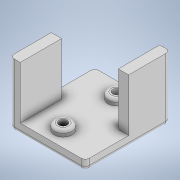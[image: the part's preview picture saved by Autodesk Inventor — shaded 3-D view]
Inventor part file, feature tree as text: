
AUTODESK INVENTOR PART (.ipt)
format: ipt  version: 2020 (Build 240168000, 168)  size: 180,224 bytes
history: native  units: in
note: dims shown in document units (in); Inventor stores cm internally (conversion verified against a paired STEP export)
features: extrude x5, sketch x5, fillet x2
ambient origin geometry x8: Origin, YZ Plane, XZ Plane, XY Plane, X Axis, Y Axis, Z Axis, Center Point
bodies: Solid1 (feature_tree)
feature tree (12):
  extrude  "Extrusion1"  Depth=1.6142in
  extrude  "Extrusion2"  Depth=0.1969in
  extrude  "Extrusion3"  Depth=0.1969in
  extrude  "Extrusion4"  Depth=1.0in TaperAngle=0.0deg
  fillet  "Fillet1"  Radius=0.3346in
  fillet  "Fillet2"  Radius=0.3346in
  extrude  "Extrusion5"  Depth=0.1181in
  sketch  "Sketch1"  dims[d0=1.4331in d1=1.6142in]
  sketch  "Sketch2"  dims[d2=0.1969in d3=0.0in d4=0.1969in]
  sketch  "Sketch3"  dims[d5=0.7874in d6=0.1969in]
  sketch  "Sketch4"  dims[d7=0.7874in d8=1.0in d9=0.0in d10=0.3346in d11=0.3346in]
  sketch  "Sketch5"  dims[d12=0.1181in d13=0.0in d14=0.1575in d15=0.1575in d16=0.3937in d17=0.0in d18=0.0787in d19=0.0591in d20=0.2362in d21=0.2362in d22=0.1181in d23=0.0in d24=0.5197in d25=0.5197in]
